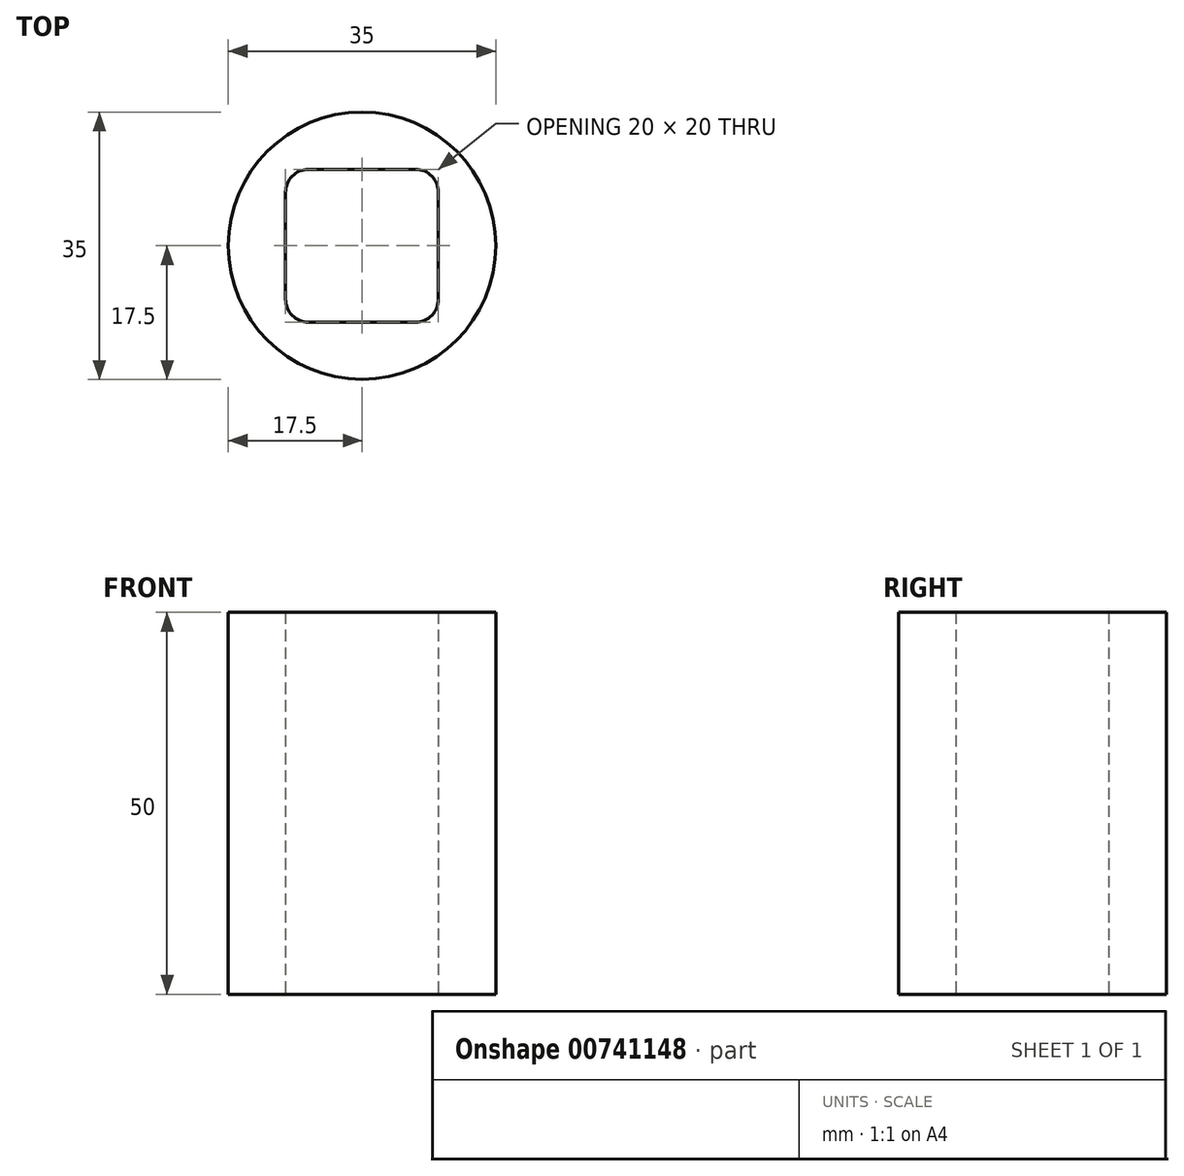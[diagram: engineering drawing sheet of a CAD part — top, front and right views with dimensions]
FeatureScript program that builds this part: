
annotation { "Feature Type Name" : "Feature", "Feature Type Description" : "" }
export const myFeature = defineFeature(function(context is Context, id is Id, definition is map)
    precondition{}
    {
        {
            var Q0;
            Q0=qCreatedBy(makeId("Top.planeOp"),FACE);
            var sketch = newSketch(context, id + "F0", { "sketchPlane" : qUnion([Q0])});
            skCircle(sketch, "E0", {"center": v(0, 0) * mm, "radius": 17.5 * mm});
            skLineSegment(sketch, "E1.bottom", {"start": v(10, -10) * mm, "end": v(-10, -10) * mm});
            skLineSegment(sketch, "E1.top", {"start": v(10, 10) * mm, "end": v(-10, 10) * mm});
            skLineSegment(sketch, "E1.left", {"start": v(10, -10) * mm, "end": v(10, 10) * mm});
            skLineSegment(sketch, "E1.right", {"start": v(-10, -10) * mm, "end": v(-10, 10) * mm});
            skSolve(sketch);
        }
        {
            var Q0;
            Q0=makeQuery(id+"F0.imprint","IMPRINT",FACE,{"disambiguationData":[TD([[makeQuery(id+"F0.imprint","IMPRINT",EDGE,{"derivedFrom":sQuery(id+"F0.wireOp",EDGE,"E0")}),1.0]])]});
            extrude(context, id + "F1", {"entities" : qUnion([Q0]), "depth" : 25 * mm, "offsetDistance" : 25 * mm, "hasSecondDirection" : true, "secondDirectionOppositeDirection" : true, "secondDirectionDepth" : 25 * mm});
        }
        {
            var Q0;
            Q0=makeQuery(id+"F1.opExtrude","SWEPT_EDGE",EDGE,{"disambiguationData":[OSD([sQuery(id+"F0.wireOp",EDGE,"E1.top"),sQuery(id+"F0.wireOp",EDGE,"E1.right")])]});
            var Q1;
            Q1=makeQuery(id+"F1.opExtrude","SWEPT_EDGE",EDGE,{"disambiguationData":[OSD([sQuery(id+"F0.wireOp",EDGE,"E1.top"),sQuery(id+"F0.wireOp",EDGE,"E1.left")])]});
            var Q2;
            Q2=makeQuery(id+"F1.opExtrude","SWEPT_EDGE",EDGE,{"disambiguationData":[OSD([sQuery(id+"F0.wireOp",EDGE,"E1.bottom"),sQuery(id+"F0.wireOp",EDGE,"E1.right")])]});
            var Q3;
            Q3=makeQuery(id+"F1.opExtrude","SWEPT_EDGE",EDGE,{"disambiguationData":[OSD([sQuery(id+"F0.wireOp",EDGE,"E1.bottom"),sQuery(id+"F0.wireOp",EDGE,"E1.left")])]});
            fillet(context, id + "F2", {"entities" : qUnion([Q0, Q1, Q2, Q3]), "radius" : 3 * mm, "tangentPropagation" : true, "allowEdgeOverflow" : false});
        }
    });
